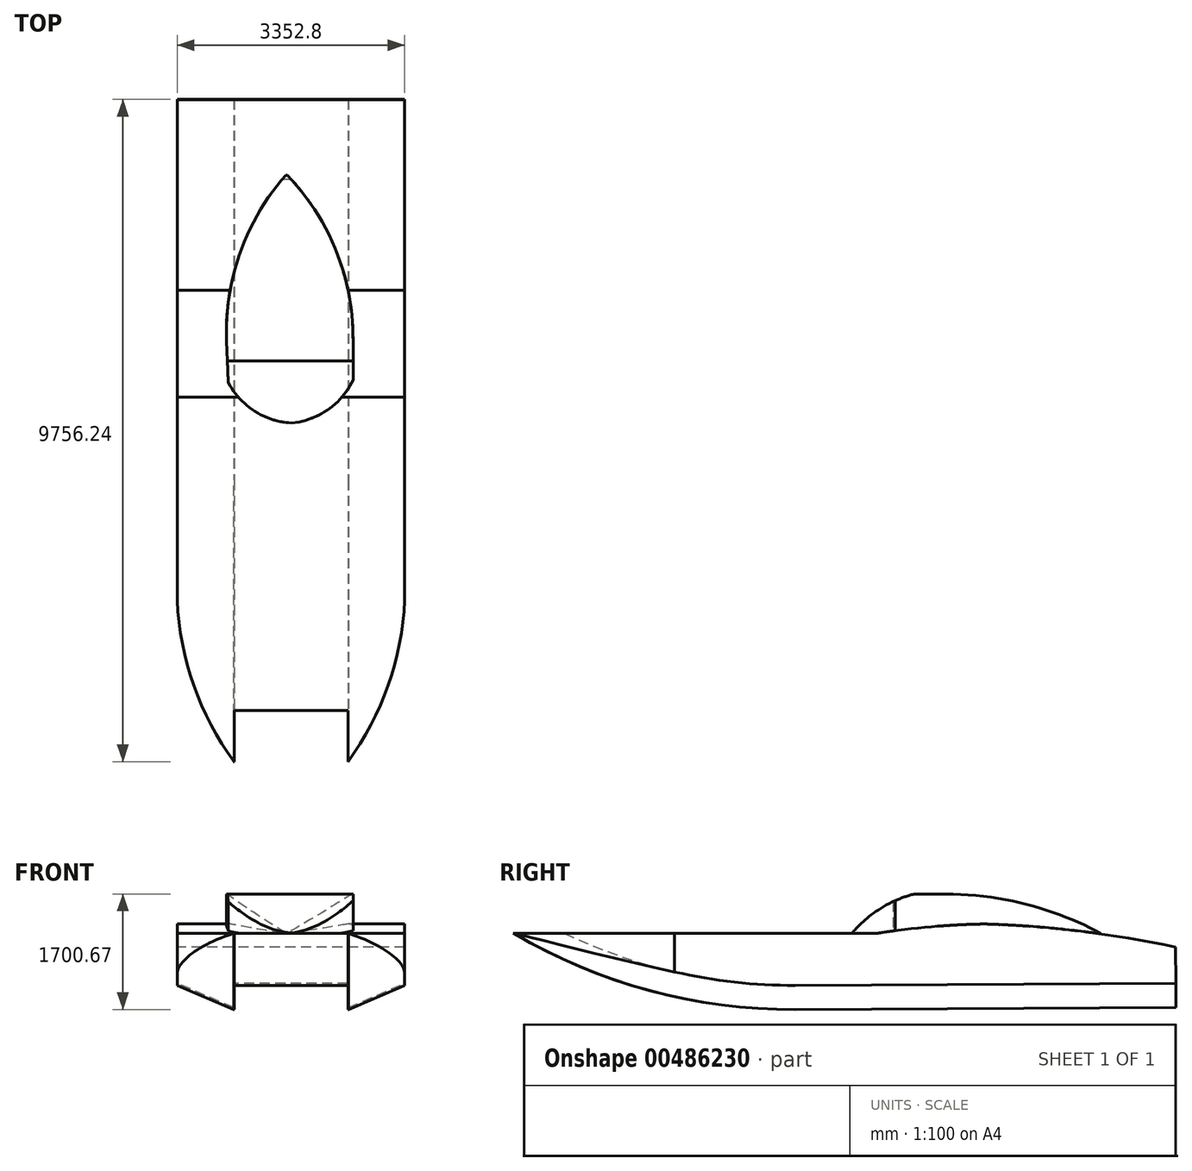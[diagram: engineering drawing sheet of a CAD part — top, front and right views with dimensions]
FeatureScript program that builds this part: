
annotation { "Feature Type Name" : "Feature", "Feature Type Description" : "" }
export const myFeature = defineFeature(function(context is Context, id is Id, definition is map)
    precondition{}
    {
        {
            var Q0;
            Q0=qCreatedBy(makeId("Right.planeOp"),FACE);
            var sketch = newSketch(context, id + "F0", { "sketchPlane" : qUnion([Q0])});
            skLineSegment(sketch, "E0", {"start": v(9903.4, 2819.64) * mm, "end": v(9906.18, 2286.25) * mm});
            skLineSegment(sketch, "E1", {"start": v(9906.18, 2286.25) * mm, "end": v(4296.5, 2257.1) * mm});
            skLineSegment(sketch, "E2", {"start": v(7101.34, 2271.67) * mm, "end": v(7096.72, 3160.66) * mm, "construction": true});
            skArc(sketch, "E3", {"start": v(9903.4, 2819.64) * mm, "mid": v(8507.76, 3053.5) * mm, "end": v(7096.72, 3160.66) * mm});
            skLineSegment(sketch, "E4", {"start": v(5524.18, 2263.47) * mm, "end": v(5520.22, 3025.46) * mm, "construction": true});
            skArc(sketch, "E5", {"start": v(7096.72, 3160.66) * mm, "mid": v(6306.11, 3120.55) * mm, "end": v(5520.22, 3025.46) * mm});
            skLineSegment(sketch, "E6", {"start": v(5520.22, 3025.46) * mm, "end": v(149.94, 3025.46) * mm});
            skArc(sketch, "E7", {"start": v(149.94, 3025.46) * mm, "mid": v(2186.92, 2445.37) * mm, "end": v(4296.5, 2257.1) * mm});
            skLineSegment(sketch, "E8", {"start": v(4296.5, 2257.1) * mm, "end": v(4298.35, 1901.5) * mm, "construction": true});
            skLineSegment(sketch, "E9", {"start": v(4298.35, 1901.5) * mm, "end": v(9906.18, 1930.65) * mm});
            skLineSegment(sketch, "E10", {"start": v(9906.18, 1930.65) * mm, "end": v(9906.18, 2286.25) * mm});
            skArc(sketch, "E11", {"start": v(149.94, 3025.46) * mm, "mid": v(2147.87, 2181.98) * mm, "end": v(4298.35, 1901.5) * mm});
            skSolve(sketch);
        }
        {
            var Q0;
            Q0 = qSketchRegion(id + "F0", true);
            extrude(context, id + "F1", {"entities" : qUnion([Q0]), "depth" : 3352.8 * mm, "offsetDistance" : 25.4 * mm});
        }
        {
            var Q0;
            Q0=makeQuery(id+"F1.opExtrude","SWEPT_FACE",FACE,{"disambiguationData":[OSD([sQuery(id+"F0.wireOp",EDGE,"E6")])]});
            var sketch = newSketch(context, id + "F2", { "sketchPlane" : qUnion([Q0])});
            skLineSegment(sketch, "E12", {"start": v(1676.4, 5520.22) * mm, "end": v(1676.4, 5139.22) * mm, "construction": true});
            skLineSegment(sketch, "E13", {"start": v(1676.4, 5520.22) * mm, "end": v(2590.8, 5520.22) * mm, "construction": true});
            skLineSegment(sketch, "E14", {"start": v(2590.8, 5520.22) * mm, "end": v(1676.4, 5520.22) * mm, "construction": true});
            skLineSegment(sketch, "E15", {"start": v(1676.4, 5520.22) * mm, "end": v(762, 5520.22) * mm, "construction": true});
            skLineSegment(sketch, "E16", {"start": v(1612.43, 8801.7) * mm, "end": v(1676.4, 5520.22) * mm, "construction": true});
            skLineSegment(sketch, "E17", {"start": v(2590.8, 5520.22) * mm, "end": v(2590.8, 5774.22) * mm, "construction": true});
            skLineSegment(sketch, "E18", {"start": v(2590.8, 5774.22) * mm, "end": v(2590.8, 6383.82) * mm});
            skArc(sketch, "E19", {"start": v(1676.4, 5139.22) * mm, "mid": v(2218.54, 5334.4) * mm, "end": v(2590.8, 5774.22) * mm});
            skArc(sketch, "E20.MirrorCS", {"start": v(1691.25, 5139.5) * mm, "mid": v(1141.92, 5313.42) * mm, "end": v(752.8, 5738.38) * mm});
            skLineSegment(sketch, "E21.MirrorCS", {"start": v(752.8, 5738.38) * mm, "end": v(729.04, 6347.52) * mm});
            skArc(sketch, "E22", {"start": v(1612.43, 8801.7) * mm, "mid": v(931.87, 7660.59) * mm, "end": v(729.04, 6347.52) * mm});
            skArc(sketch, "E23", {"start": v(2590.8, 6383.82) * mm, "mid": v(2336.94, 7687.98) * mm, "end": v(1612.43, 8801.7) * mm});
            skLineSegment(sketch, "E24", {"start": v(2590.8, 6383.82) * mm, "end": v(2590.8, 5774.22) * mm});
            skSolve(sketch);
        }
        {
            var Q0;
            Q0 = qSketchRegion(id + "F2", true);
            extrude(context, id + "F3", {"entities" : qUnion([Q0]), "operationType" : NewBodyOperationType.ADD, "depth" : 914.4 * mm, "offsetDistance" : 25.4 * mm});
        }
        {
            var Q0;
            Q0=makeQuery(id+"F1.opExtrude","CAP_FACE",FACE,{"disambiguationData":[OSD([sQuery(id+"F0.wireOp",EDGE,"E0"),sQuery(id+"F0.wireOp",EDGE,"E1"),sQuery(id+"F0.wireOp",EDGE,"E3"),sQuery(id+"F0.wireOp",EDGE,"E5"),sQuery(id+"F0.wireOp",EDGE,"E6"),sQuery(id+"F0.wireOp",EDGE,"E7")])],"isStart":false});
            var sketch = newSketch(context, id + "F4", { "sketchPlane" : qUnion([Q0])});
            skArc(sketch, "E25", {"start": v(6051.27, 3602.06) * mm, "mid": v(5549.4, 3384.98) * mm, "end": v(5137.42, 3025.46) * mm});
            skLineSegment(sketch, "E26", {"start": v(6051.27, 3602.06) * mm, "end": v(6508.47, 3602.06) * mm});
            skLineSegment(sketch, "E27", {"start": v(5137.42, 3025.46) * mm, "end": v(5137.42, 4052.91) * mm});
            skLineSegment(sketch, "E28", {"start": v(5137.42, 4052.91) * mm, "end": v(8976.57, 4052.91) * mm});
            skArc(sketch, "E29", {"start": v(8816.33, 3012.9) * mm, "mid": v(7699.4, 3452.45) * mm, "end": v(6508.47, 3602.06) * mm});
            skLineSegment(sketch, "E30", {"start": v(8816.33, 3012.9) * mm, "end": v(8976.57, 4052.91) * mm});
            skSolve(sketch);
        }
        {
            var Q0;
            Q0 = qSketchRegion(id + "F4", true);
            extrude(context, id + "F5", {"entities" : qUnion([Q0]), "operationType" : NewBodyOperationType.REMOVE, "oppositeDirection" : true, "depth" : 3352.8 * mm, "offsetDistance" : 25.4 * mm});
        }
        {
            var Q0;
            Q0=makeQuery(id+"F1.opExtrude","SWEPT_FACE",FACE,{"disambiguationData":[OSD([sQuery(id+"F0.wireOp",EDGE,"E0")])]});
            var sketch = newSketch(context, id + "F6", { "sketchPlane" : qUnion([Q0])});
            skSolve(sketch);
        }
        {
            var Q0;
            Q0=makeQuery(id+"F1.opExtrude","SWEPT_FACE",FACE,{"disambiguationData":[OSD([sQuery(id+"F0.wireOp",EDGE,"E10")])]});
            var sketch = newSketch(context, id + "F7", { "sketchPlane" : qUnion([Q0])});
            skLineSegment(sketch, "E31", {"start": v(-1676.4, 2286.25) * mm, "end": v(0, 2286.25) * mm, "construction": true});
            skLineSegment(sketch, "E32", {"start": v(0, 2286.25) * mm, "end": v(-1676.4, 2286.25) * mm, "construction": true});
            skLineSegment(sketch, "E33", {"start": v(-1676.4, 2286.25) * mm, "end": v(-3352.8, 2286.25) * mm, "construction": true});
            skLineSegment(sketch, "E34", {"start": v(-1676.4, 2286.25) * mm, "end": v(-838.2, 2286.25) * mm, "construction": true});
            skLineSegment(sketch, "E35", {"start": v(-838.2, 2286.25) * mm, "end": v(-1676.4, 2286.25) * mm, "construction": true});
            skLineSegment(sketch, "E36", {"start": v(-1676.4, 2286.25) * mm, "end": v(-2514.6, 2286.25) * mm, "construction": true});
            skLineSegment(sketch, "E37", {"start": v(-2514.6, 2286.25) * mm, "end": v(-2514.6, 1930.65) * mm});
            skLineSegment(sketch, "E38", {"start": v(-838.2, 2286.25) * mm, "end": v(-838.2, 1930.65) * mm});
            skLineSegment(sketch, "E39", {"start": v(-3352.8, 1742.88) * mm, "end": v(-3352.8, 2286.25) * mm});
            skLineSegment(sketch, "E40", {"start": v(-2514.6, 1930.65) * mm, "end": v(-2514.6, 1742.88) * mm});
            skLineSegment(sketch, "E41", {"start": v(-2514.6, 1742.88) * mm, "end": v(-838.2, 1742.88) * mm});
            skLineSegment(sketch, "E42", {"start": v(-838.2, 1742.88) * mm, "end": v(-838.2, 1930.65) * mm});
            skLineSegment(sketch, "E43", {"start": v(0, 2286.25) * mm, "end": v(381.6, 2006.47) * mm});
            skLineSegment(sketch, "E44", {"start": v(-838.2, 1742.88) * mm, "end": v(192.5, 1742.88) * mm});
            skLineSegment(sketch, "E45", {"start": v(192.5, 1742.88) * mm, "end": v(381.6, 2006.47) * mm});
            skLineSegment(sketch, "E46", {"start": v(-3352.8, 1742.88) * mm, "end": v(-2514.6, 1742.88) * mm});
            skLineSegment(sketch, "E47", {"start": v(-838.2, 1930.65) * mm, "end": v(-831.85, 1930.65) * mm});
            skLineSegment(sketch, "E48", {"start": v(-831.85, 1930.65) * mm, "end": v(0, 2286.25) * mm});
            skLineSegment(sketch, "E49", {"start": v(-1676.4, 2286.25) * mm, "end": v(-1676.4, 1972.3) * mm, "construction": true});
            skLineSegment(sketch, "E50.MirrorCS", {"start": v(-2514.6, 1930.65) * mm, "end": v(-2520.95, 1930.65) * mm});
            skLineSegment(sketch, "E51.MirrorCS", {"start": v(-2520.95, 1930.65) * mm, "end": v(-3352.8, 2286.25) * mm});
            skSolve(sketch);
        }
        {
            var Q0;
            {var subQ0=sQuery(id+"F7.wireOp",EDGE,"E51.MirrorCS");Q0=makeQuery(id+"F7.imprint","IMPRINT",FACE,{"disambiguationData":[TD([[makeQuery(id+"F7.imprint","IMPRINT",EDGE,{"derivedFrom":subQ0}),1.0]])]});}
            var Q1;
            Q1=makeQuery(id+"F7.imprint","IMPRINT",FACE,{"disambiguationData":[TD([[makeQuery(id+"F7.imprint","IMPRINT",EDGE,{"derivedFrom":sQuery(id+"F7.wireOp",EDGE,"E40")}),-1.0]])]});
            var Q2;
            {var subQ0=sQuery(id+"F7.wireOp",EDGE,"E40");Q2=makeQuery(id+"F7.imprint","IMPRINT",FACE,{"disambiguationData":[TD([[makeQuery(id+"F7.imprint","IMPRINT",EDGE,{"derivedFrom":subQ0}),1.0]])]});}
            var Q3;
            Q3=makeQuery(id+"F7.imprint","IMPRINT",FACE,{"disambiguationData":[TD([[makeQuery(id+"F7.imprint","IMPRINT",EDGE,{"derivedFrom":sQuery(id+"F7.wireOp",EDGE,"E42")}),-1.0]])]});
            var Q4;
            {var subQ0=sQuery(id+"F7.wireOp",EDGE,"E48");Q4=makeQuery(id+"F7.imprint","IMPRINT",FACE,{"disambiguationData":[TD([[makeQuery(id+"F7.imprint","IMPRINT",EDGE,{"derivedFrom":subQ0}),-1.0]])]});}
            var Q5;
            {var subQ0=sQuery(id+"F7.wireOp",EDGE,"E37");Q5=makeQuery(id+"F7.imprint","IMPRINT",FACE,{"disambiguationData":[TD([[makeQuery(id+"F7.imprint","IMPRINT",EDGE,{"derivedFrom":subQ0}),1.0]])]});}
            var Q6;
            Q6=makeQuery(id+"F1.opExtrude","CAP_EDGE",EDGE,{"disambiguationData":[OSD([sQuery(id+"F0.wireOp",EDGE,"E9")])],"isStart":false});
            var Q7;
            Q7=makeQuery(id+"F1.opExtrude","CAP_EDGE",EDGE,{"disambiguationData":[OSD([sQuery(id+"F0.wireOp",EDGE,"E11")])],"isStart":false});
            sweep(context, id + "F8", {"operationType" : NewBodyOperationType.REMOVE, "profiles" : qUnion([Q0, Q1, Q2, Q3, Q4, Q5]), "path" : qUnion([Q6, Q7])});
        }
        {
            var Q0;
            Q0=makeQuery(id+"F1.opExtrude","SWEPT_FACE",FACE,{"disambiguationData":[OSD([sQuery(id+"F0.wireOp",EDGE,"E6")])]});
            var sketch = newSketch(context, id + "F9", { "sketchPlane" : qUnion([Q0])});
            skArc(sketch, "E52", {"start": v(0, 2933.73) * mm, "mid": v(180.65, 1470.04) * mm, "end": v(838.2, 149.94) * mm});
            skLineSegment(sketch, "E53", {"start": v(1676.4, 901.53) * mm, "end": v(1676.4, 2869.19) * mm, "construction": true});
            skArc(sketch, "E54.MirrorCS", {"start": v(3352.8, 2933.73) * mm, "mid": v(3172.15, 1470.04) * mm, "end": v(2514.6, 149.94) * mm});
            skLineSegment(sketch, "E55", {"start": v(0, 2933.73) * mm, "end": v(-833.76, 377.76) * mm, "construction": true});
            skLineSegment(sketch, "E56", {"start": v(-833.76, 377.76) * mm, "end": v(0, 2933.73) * mm});
            skLineSegment(sketch, "E57", {"start": v(-833.76, 377.76) * mm, "end": v(838.2, 149.94) * mm});
            skLineSegment(sketch, "E58", {"start": v(2520.95, 149.94) * mm, "end": v(4820.35, 149.94) * mm});
            skLineSegment(sketch, "E59", {"start": v(4820.35, 149.94) * mm, "end": v(3352.8, 2933.73) * mm});
            skSolve(sketch);
        }
        {
            var Q0;
            Q0 = qSketchRegion(id + "F9", true);
            var Q1;
            Q1=makeQuery(id+"F9.imprint","IMPRINT",FACE,{"disambiguationData":[TD([[makeQuery(id+"F9.imprint","IMPRINT",EDGE,{"derivedFrom":sQuery(id+"F9.wireOp",EDGE,"E58")}),1.0]])]});
            var Q2;
            {var subQ1=sQuery(id+"F0.wireOp",EDGE,"E6");var subQ2=makeQuery(id+"F1.opExtrude","SWEPT_FACE",FACE,{"disambiguationData":[OSD([subQ1])]});var subQ4=sQuery(id+"F0.wireOp",EDGE,"E11");var subQ5=makeQuery(id+"F8.opSweep","SWEPT_FACE",FACE,{"disambiguationData":[OSD([subQ4,sQuery(id+"F7.wireOp",EDGE,"E51.MirrorCS")])]});var subQ7=subQ2;var subQ10=makeQuery(id+"F8.boolean.opBoolean","INTERSECT",EDGE,{"derivedFrom":[subQ7,subQ5]});Q2=makeQuery(id+"F9.imprint","IMPRINT",FACE,{"disambiguationData":[TD([[makeQuery(id+"F9.imprint","IMPRINT",EDGE,{"derivedFrom":subQ10}),1.0]])]});}
            extrude(context, id + "F10", {"entities" : qUnion([Q0, Q1, Q2]), "operationType" : NewBodyOperationType.REMOVE, "oppositeDirection" : true, "depth" : 1320.8 * mm, "offsetDistance" : 25.4 * mm});
        }
    });
